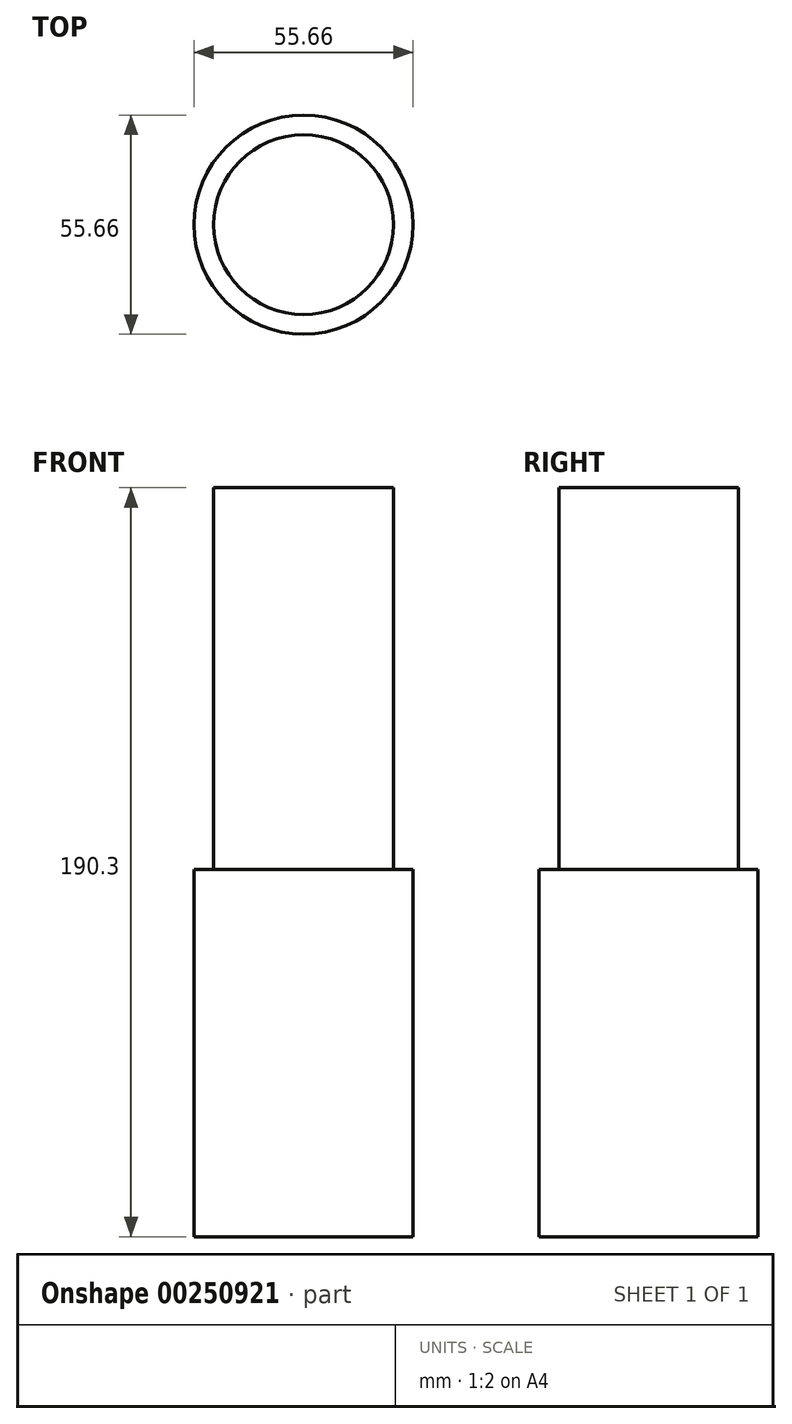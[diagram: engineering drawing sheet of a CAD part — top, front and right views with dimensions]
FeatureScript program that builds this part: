
annotation { "Feature Type Name" : "Feature", "Feature Type Description" : "" }
export const myFeature = defineFeature(function(context is Context, id is Id, definition is map)
    precondition{}
    {
        {
            var Q0;
            Q0=qCreatedBy(makeId("Front.planeOp"),FACE);
            var sketch = newSketch(context, id + "F0", { "sketchPlane" : qUnion([Q0])});
            skLineSegment(sketch, "E0.bottom", {"start": v(-27.83, 46.62) * mm, "end": v(27.83, 46.62) * mm});
            skLineSegment(sketch, "E0.top", {"start": v(-27.83, -46.62) * mm, "end": v(27.83, -46.62) * mm});
            skLineSegment(sketch, "E0.left", {"start": v(-27.83, 46.62) * mm, "end": v(-27.83, -46.62) * mm});
            skLineSegment(sketch, "E0.right", {"start": v(27.83, 46.62) * mm, "end": v(27.83, -46.62) * mm});
            skPoint(sketch, "E0.middle", {"position": v(0, 0) * mm});
            skLineSegment(sketch, "E1", {"start": v(0, 46.62) * mm, "end": v(0, -46.62) * mm});
            skPoint(sketch, "E1.endSnap0", {"position": v(0, -46.62) * mm});
            skSolve(sketch);
        }
        {
            var Q0;
            {var subQ0=sQuery(id+"F0.wireOp",EDGE,"E0.left");Q0=makeQuery(id+"F0.imprint","IMPRINT",FACE,{"disambiguationData":[TD([[makeQuery(id+"F0.imprint","IMPRINT",EDGE,{"derivedFrom":subQ0}),1.0]])]});}
            var Q1;
            Q1=sQuery(id+"F0.wireOp",EDGE,"E1");
            revolve(context, id + "F1", {"entities" : qUnion([Q0]), "axis" : qUnion([Q1]), "revolveType" : RevolveType.FULL});
        }
        {
            var Q0;
            Q0=makeQuery(id+"F1.opRevolve","SWEPT_FACE",FACE,{"disambiguationData":[OSD([sQuery(id+"F0.wireOp",EDGE,"E0.bottom")])]});
            shell(context, id + "F2", {"entities" : qUnion([Q0]), "thickness" : 5 * mm});
        }
        {
            var Q0;
            Q0=makeQuery(id+"F2.opShell","OFFSET_FACE",FACE,{"disambiguationData":[OSD([sQuery(id+"F0.wireOp",EDGE,"E0.top")])]});
            extrude(context, id + "F3", {"entities" : qUnion([Q0]), "operationType" : NewBodyOperationType.ADD, "depth" : 185.3 * mm});
        }
    });
